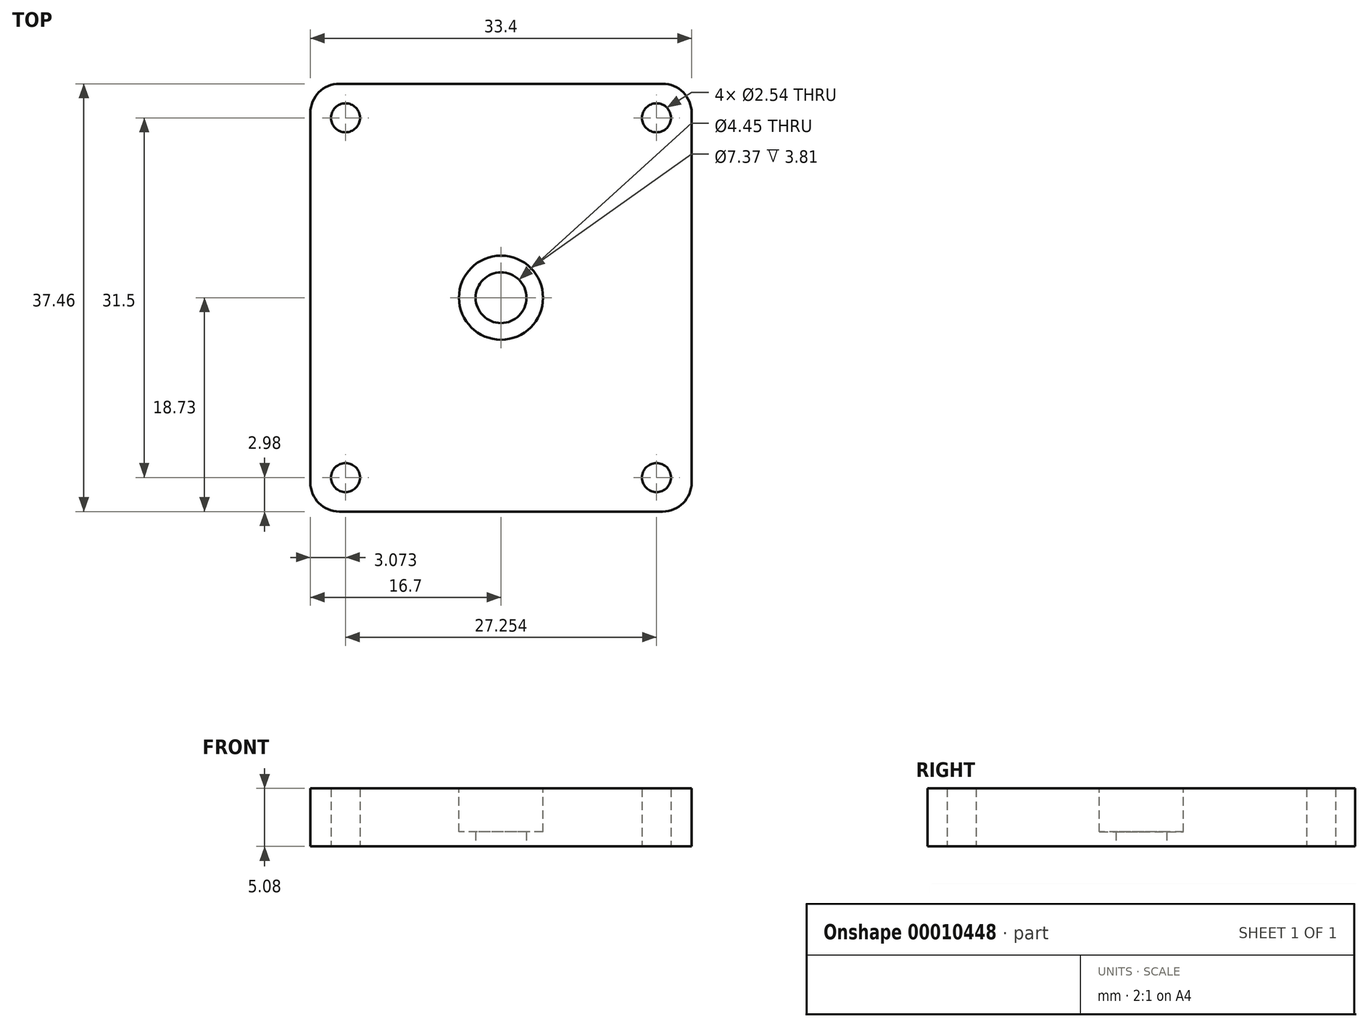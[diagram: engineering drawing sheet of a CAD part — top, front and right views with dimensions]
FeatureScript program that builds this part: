
annotation { "Feature Type Name" : "Feature", "Feature Type Description" : "" }
export const myFeature = defineFeature(function(context is Context, id is Id, definition is map)
    precondition{}
    {
        {
            var Q0;
            Q0=qCreatedBy(makeId("Top.planeOp"),FACE);
            var sketch = newSketch(context, id + "F0", { "sketchPlane" : qUnion([Q0])});
            skLineSegment(sketch, "E0.rect.bottom", {"start": v(16.7, 18.73) * mm, "end": v(-16.7, 18.73) * mm});
            skLineSegment(sketch, "E0.rect.top", {"start": v(16.7, -18.73) * mm, "end": v(-16.7, -18.73) * mm});
            skLineSegment(sketch, "E0.rect.left", {"start": v(16.7, 18.73) * mm, "end": v(16.7, -18.73) * mm});
            skLineSegment(sketch, "E0.rect.right", {"start": v(-16.7, 18.73) * mm, "end": v(-16.7, -18.73) * mm});
            skPoint(sketch, "E0.rect.middle", {"position": v(0, 0) * mm});
            skLineSegment(sketch, "E1.rect.bottom", {"start": v(13.63, 15.75) * mm, "end": v(-13.63, 15.75) * mm, "construction": true});
            skLineSegment(sketch, "E1.rect.top", {"start": v(13.63, -15.75) * mm, "end": v(-13.63, -15.75) * mm, "construction": true});
            skLineSegment(sketch, "E1.rect.left", {"start": v(13.63, 15.75) * mm, "end": v(13.63, -15.75) * mm, "construction": true});
            skLineSegment(sketch, "E1.rect.right", {"start": v(-13.63, 15.75) * mm, "end": v(-13.63, -15.75) * mm, "construction": true});
            skCircle(sketch, "E2", {"center": v(-13.63, 15.75) * mm, "radius": 1.27 * mm});
            skCircle(sketch, "E3", {"center": v(13.63, 15.75) * mm, "radius": 1.27 * mm});
            skCircle(sketch, "E4", {"center": v(13.63, -15.75) * mm, "radius": 1.27 * mm});
            skCircle(sketch, "E5", {"center": v(-13.63, -15.75) * mm, "radius": 1.27 * mm});
            skCircle(sketch, "E6", {"center": v(0, 0) * mm, "radius": 2.22 * mm});
            skSolve(sketch);
        }
        {
            var Q0;
            Q0 = qSketchRegion(id + "F0", true);
            extrude(context, id + "F1", {"entities" : qUnion([Q0]), "depth" : 5.08 * mm});
        }
        {
            var Q0;
            Q0=makeQuery(id+"F1.opExtrude","CAP_FACE",FACE,{"disambiguationData":[OSD([sQuery(id+"F0.wireOp",EDGE,"E0.rect.bottom"),sQuery(id+"F0.wireOp",EDGE,"E0.rect.top"),sQuery(id+"F0.wireOp",EDGE,"E0.rect.left"),sQuery(id+"F0.wireOp",EDGE,"E0.rect.right"),sQuery(id+"F0.wireOp",EDGE,"E2"),sQuery(id+"F0.wireOp",EDGE,"E3"),sQuery(id+"F0.wireOp",EDGE,"E4"),sQuery(id+"F0.wireOp",EDGE,"E5"),sQuery(id+"F0.wireOp",EDGE,"E6")])],"isStart":false});
            var sketch = newSketch(context, id + "F2", { "sketchPlane" : qUnion([Q0])});
            skCircle(sketch, "E7", {"center": v(0, 0) * mm, "radius": 3.68 * mm});
            skSolve(sketch);
        }
        {
            var Q0;
            Q0 = qSketchRegion(id + "F2", true);
            extrude(context, id + "F3", {"entities" : qUnion([Q0]), "operationType" : NewBodyOperationType.REMOVE, "oppositeDirection" : true, "depth" : 3.8 * mm});
        }
        {
            var Q0;
            Q0=makeQuery(id+"F1.opExtrude","SWEPT_EDGE",EDGE,{"disambiguationData":[OSD([sQuery(id+"F0.wireOp",EDGE,"E0.rect.top"),sQuery(id+"F0.wireOp",EDGE,"E0.rect.left")])]});
            var Q1;
            Q1=makeQuery(id+"F1.opExtrude","SWEPT_EDGE",EDGE,{"disambiguationData":[OSD([sQuery(id+"F0.wireOp",EDGE,"E0.rect.bottom"),sQuery(id+"F0.wireOp",EDGE,"E0.rect.left")])]});
            var Q2;
            Q2=makeQuery(id+"F1.opExtrude","SWEPT_EDGE",EDGE,{"disambiguationData":[OSD([sQuery(id+"F0.wireOp",EDGE,"E0.rect.top"),sQuery(id+"F0.wireOp",EDGE,"E0.rect.right")])]});
            var Q3;
            Q3=makeQuery(id+"F1.opExtrude","SWEPT_EDGE",EDGE,{"disambiguationData":[OSD([sQuery(id+"F0.wireOp",EDGE,"E0.rect.bottom"),sQuery(id+"F0.wireOp",EDGE,"E0.rect.right")])]});
            fillet(context, id + "F4", {"entities" : qUnion([Q0, Q1, Q2, Q3]), "radius" : 2.54 * mm, "tangentPropagation" : true, "allowEdgeOverflow" : false});
        }
    });
